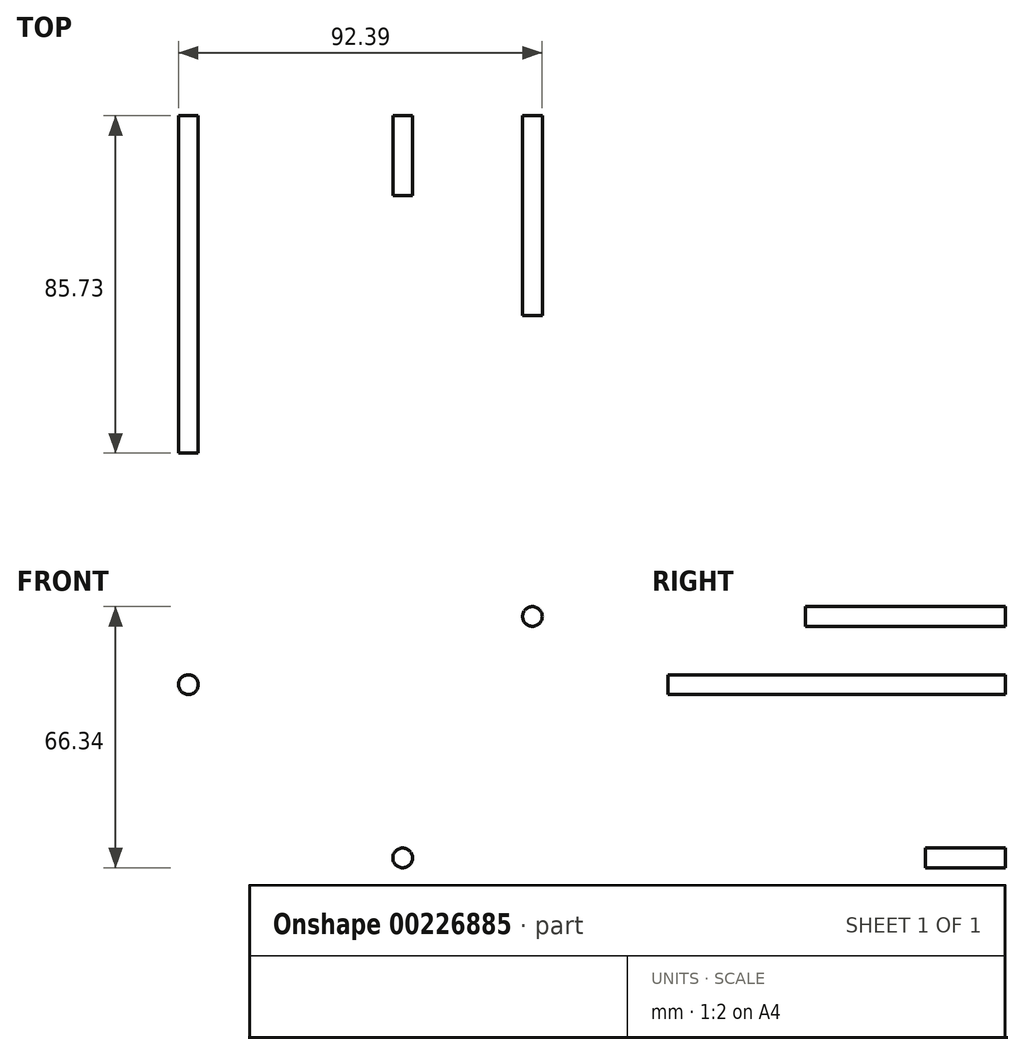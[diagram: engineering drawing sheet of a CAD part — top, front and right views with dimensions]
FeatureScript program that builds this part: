
annotation { "Feature Type Name" : "Feature", "Feature Type Description" : "" }
export const myFeature = defineFeature(function(context is Context, id is Id, definition is map)
    precondition{}
    {
        {
            var Q0;
            Q0=qCreatedBy(makeId("Front.planeOp"),FACE);
            var sketch = newSketch(context, id + "F0", { "sketchPlane" : qUnion([Q0])});
            skCircle(sketch, "E0", {"center": v(0, 0) * mm, "radius": 2.5 * mm});
            skSolve(sketch);
        }
        {
            var Q0;
            Q0=qSketchRegion(id+"F0",true);
            extrude(context, id + "F1", {"entities" : qUnion([Q0]), "depth" : 20.32 * mm});
        }
        {
            var Q0;
            Q0=qCreatedBy(makeId("Front.planeOp"),FACE);
            var sketch = newSketch(context, id + "F2", { "sketchPlane" : qUnion([Q0])});
            skCircle(sketch, "E1", {"center": v(-54.43, 44.03) * mm, "radius": 2.5 * mm});
            skSolve(sketch);
        }
        {
            var Q0;
            Q0=qSketchRegion(id+"F2",true);
            extrude(context, id + "F3", {"entities" : qUnion([Q0]), "depth" : 85.72 * mm});
        }
        {
            var Q0;
            Q0=qCreatedBy(makeId("Front.planeOp"),FACE);
            var sketch = newSketch(context, id + "F4", { "sketchPlane" : qUnion([Q0])});
            skCircle(sketch, "E2", {"center": v(32.96, 61.34) * mm, "radius": 2.5 * mm});
            skSolve(sketch);
        }
        {
            var Q0;
            Q0=qSketchRegion(id+"F4",true);
            extrude(context, id + "F5", {"entities" : qUnion([Q0]), "depth" : 50.8 * mm});
        }
    });
